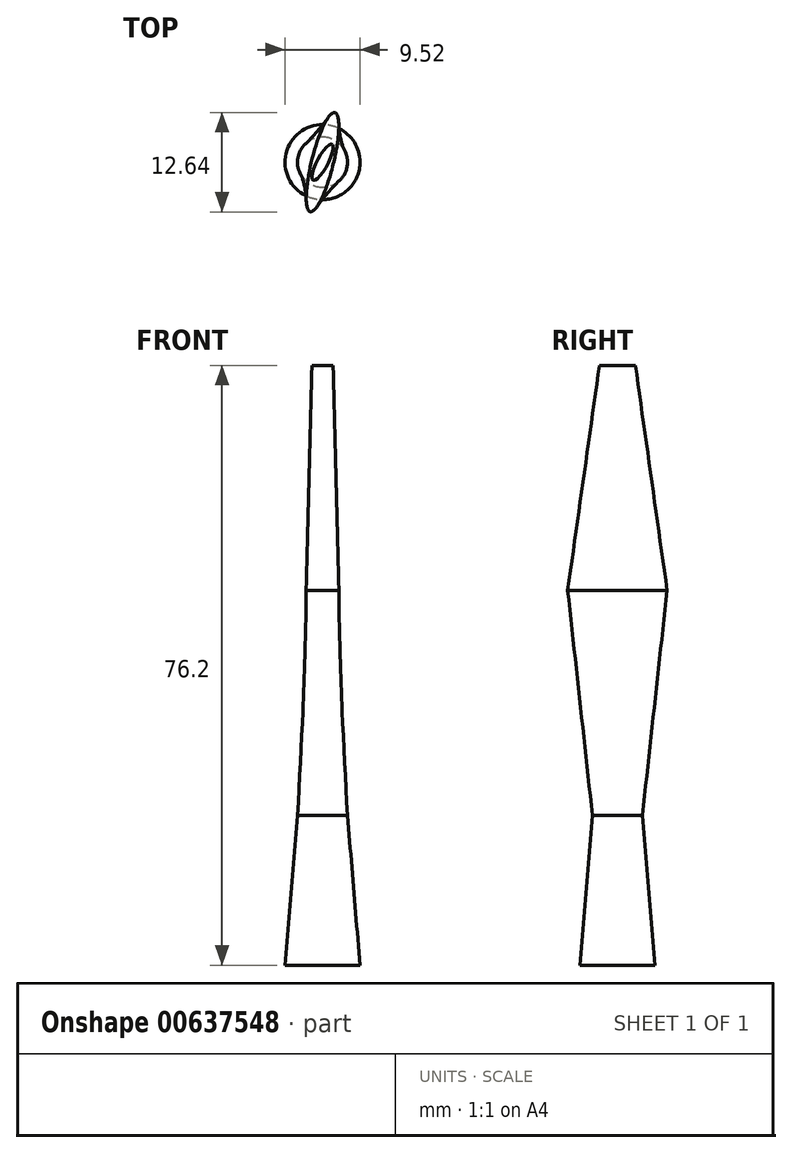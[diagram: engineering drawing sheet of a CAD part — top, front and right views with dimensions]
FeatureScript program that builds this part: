
annotation { "Feature Type Name" : "Feature", "Feature Type Description" : "" }
export const myFeature = defineFeature(function(context is Context, id is Id, definition is map)
    precondition{}
    {
        {
            var Q0;
            Q0=qCreatedBy(makeId("Top.planeOp"),FACE);
            cPlane(context, id + "F0", {"entities" : qUnion([Q0]), "cplaneType" : CPlaneType.OFFSET, "offset" : 76.2 * mm, "width" : 150 * mm, "height" : 150 * mm});
        }
        {
            var Q0;
            Q0=qCreatedBy(makeId("Top.planeOp"),FACE);
            var sketch = newSketch(context, id + "F1", { "sketchPlane" : qUnion([Q0])});
            skCircle(sketch, "E0", {"center": v(0, 0) * mm, "radius": 4.76 * mm});
            skSolve(sketch);
        }
        {
            var Q0;
            Q0=qCreatedBy(makeId("Top.planeOp"),FACE);
            cPlane(context, id + "F2", {"entities" : qUnion([Q0]), "cplaneType" : CPlaneType.OFFSET, "offset" : 19.05 * mm, "width" : 150 * mm, "height" : 150 * mm});
        }
        {
            var Q0;
            Q0=qCreatedBy(id+"F2.planeOp",FACE);
            var sketch = newSketch(context, id + "F3", { "sketchPlane" : qUnion([Q0])});
            skCircle(sketch, "E1", {"center": v(0, 0) * mm, "radius": 3.18 * mm});
            skLineSegment(sketch, "E2", {"start": v(0, 3.18) * mm, "end": v(0, -3.18) * mm, "construction": true});
            skSolve(sketch);
        }
        {
            var Q0;
            Q0=makeQuery(id+"F1.imprint","IMPRINT",FACE,{"disambiguationData":[TD([[makeQuery(id+"F1.imprint","IMPRINT",EDGE,{"derivedFrom":sQuery(id+"F1.wireOp",EDGE,"E0")}),1.0]])]});
            var Q1;
            Q1=makeQuery(id+"F3.imprint","IMPRINT",FACE,{"disambiguationData":[TD([[makeQuery(id+"F3.imprint","IMPRINT",EDGE,{"derivedFrom":sQuery(id+"F3.wireOp",EDGE,"E1")}),1.0]])]});
            loft(context, id + "F4", {"sheetProfilesArray" : [{ "sheetProfileEntities" : qUnion([Q0]) }, { "sheetProfileEntities" : qUnion([Q1]) }]});
        }
        {
            var Q0;
            Q0=makeQuery(id+"F4.opLoft","CAP_FACE",FACE,{"disambiguationData":[OSD([makeQuery(id+"F3.imprint","IMPRINT",FACE,{"disambiguationData":[TD([[makeQuery(id+"F3.imprint","IMPRINT",EDGE,{"derivedFrom":sQuery(id+"F3.wireOp",EDGE,"E1")}),1.0]])]})])],"isStart":true});
            cPlane(context, id + "F5", {"entities" : qUnion([Q0]), "cplaneType" : CPlaneType.OFFSET, "offset" : 28.57 * mm, "width" : 150 * mm, "height" : 150 * mm});
        }
        {
            var Q0;
            Q0=qCreatedBy(id+"F5.planeOp",FACE);
            var sketch = newSketch(context, id + "F6", { "sketchPlane" : qUnion([Q0])});
            skEllipse(sketch, "E3", {"center": v(0, 0) * mm, "majorRadius": 6.5 * mm, "minorRadius": 1.39 * mm, "majorAxis": v(0.24, 0.97)});
            skLineSegment(sketch, "E4", {"start": v(1.57, 6.3) * mm, "end": v(-1.57, -6.3) * mm, "construction": true});
            skSolve(sketch);
        }
        {
            var Q0;
            Q0=qCreatedBy(id+"F0.planeOp",FACE);
            var sketch = newSketch(context, id + "F7", { "sketchPlane" : qUnion([Q0])});
            skEllipse(sketch, "E5", {"center": v(0, 0) * mm, "majorRadius": 2.57 * mm, "minorRadius": 0.7 * mm, "majorAxis": v(0.47, 0.88)});
            skLineSegment(sketch, "E6", {"start": v(1.2, 2.27) * mm, "end": v(-1.2, -2.27) * mm, "construction": true});
            skSolve(sketch);
        }
        {
            var Q0;
            Q0=makeQuery(id+"F3.imprint","IMPRINT",FACE,{"disambiguationData":[TD([[makeQuery(id+"F3.imprint","IMPRINT",EDGE,{"derivedFrom":sQuery(id+"F3.wireOp",EDGE,"E1")}),1.0]])]});
            var Q1;
            Q1=makeQuery(id+"F6.imprint","IMPRINT",FACE,{"disambiguationData":[TD([[makeQuery(id+"F6.imprint","IMPRINT",EDGE,{"derivedFrom":sQuery(id+"F6.wireOp",EDGE,"E3")}),1.0]])]});
            loft(context, id + "F8", {"sheetProfilesArray" : [{ "sheetProfileEntities" : qUnion([Q0]) }, { "sheetProfileEntities" : qUnion([Q1]) }]});
        }
        {
            var Q1;
            Q1=makeQuery(id+"F8.opLoft","CAP_FACE",FACE,{"disambiguationData":[OSD([makeQuery(id+"F6.imprint","IMPRINT",FACE,{"disambiguationData":[TD([[makeQuery(id+"F6.imprint","IMPRINT",EDGE,{"derivedFrom":sQuery(id+"F6.wireOp",EDGE,"E3")}),1.0]])]})])],"isStart":true});
            var Q2;
            Q2=makeQuery(id+"F7.imprint","IMPRINT",FACE,{"disambiguationData":[TD([[makeQuery(id+"F7.imprint","IMPRINT",EDGE,{"derivedFrom":sQuery(id+"F7.wireOp",EDGE,"E5")}),1.0]])]});
            loft(context, id + "F9", {"operationType" : NewBodyOperationType.ADD, "sheetProfilesArray" : [{ "sheetProfileEntities" : qUnion([Q1]) }, { "sheetProfileEntities" : qUnion([Q2]) }]});
        }
    });
